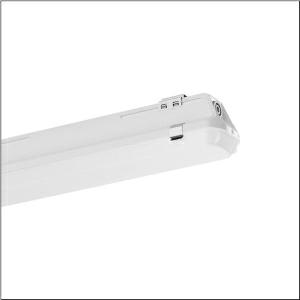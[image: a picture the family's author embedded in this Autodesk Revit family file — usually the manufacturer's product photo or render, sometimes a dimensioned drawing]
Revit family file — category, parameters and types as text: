
# Revit family: monsun_r__11_51fp10ep460h_f2a9
name_source: partatom
category: Lighting Fixtures
units: mm (PartAtom-declared; Revit-internal decimal feet)

## family parameters
Cut with Voids When Loaded = No
Host = Face
Light Source = No
Part Type = Normal
Room Calculation Point = No
Round Connector Dimension = Use Diameter
Shared = No

## types (1)
- --- (1 x LED, 6050 lm, 34.6 W, 4000K)
    Apparent Load = 35 VA
    CIE Flux Codes = 47 77 93 94 100
    Color Rendering = 80
    Color Temperature = 4000K
    Default Elevation = 1800 mm
    Description = Monsun® 11, damp-proof luminaire, chain hanger, primary optical cover: enclosure, of PMMA, light emission: direct distribution, primary light characteristic: symmetric, installation type: suspended mounting, surface-mounted, horizontal mounting, vertical mounting, LED, rated luminous flux: 6.050lm, luminous efficacy: 175lm/W, light colour: 840, colour temperature: 4000K, control gear: ECG DALI, with terminal, 5-pole, max. 2.5mm², mains connection: 220..240V, AC, 50/60Hz, rated input power: 35W, luminaire housing, of glass-fibre reinforced polyester, uncoated, bright grey, incl. chain hanger, length: 1.590mm, width: 90mm, height: 88mm, clip for enclosure, of stainless steel (V2A), ceiling mounting element, of stainless steel (V2A), chain hanger, of stainless steel (V2A), protection rating (complete): IP66, insulation class (complete): insulation class I (protective earthing), certification: CE, ENEC, VDE, UKCA, protection symbol: D, impact resistance: IK04, permissible operating ambient temperature: -25..+40°C, standard: EN 50419, EN 60598-2-1, no direct snow, no direct sun, no direct rain, for indoor or canopied outdoor use, corresponds to IFS (International Featured Standards) requirements for safety and quality in the food industry, contact your sales advisor before using the luminaires in applications with unclear chemical exposure, large temperature fluctuations or condensation-forming humidity, LABS conformity tested according to VDMA 24364:2018-05, packaging unit: 1 piece
    Height = 89 mm
    Lamp = 1 x LED
    Lamp Light Flux = 6050 lm
    Lamp Power = 34.6 W
    Lamp count = 1
    Length = 1590 mm
    Luminous efficacy = 175 lm/W
    Manufacturer = Siteco
    ModVariant = No
    Model = 51FP10EP460H
    Mounting Place = Ceiling
    Mounting Type = Surface mounted
    Number of Poles = 1
    OnlyDefault = Yes
    Power Factor = 1
    Product Name = Monsun® 11
    Product group = damp-proof luminaire
    ProductGroupID = 301
    Protection Class = Protection class I
    Protection Degree = IP 66
    RLX_Detail_Level = 1
    RLX_Emergency_Light_Flux = 0 lm
    RLX_Emergency_Type = 0
    RLX_Emergency_Type_DB = No
    RlxData = <blob elided: 92425 chars, md5=b4d11d01>
    Socket = socket
    Standby Power = 0 W
    System Light Flux = 6050 lm
    System Power = 35 W
    Type Comments = factory setting: luminous flux: 100 % | dim-lin: 254 | 232 mA
    Type Image = l_1004748.jpg
    URL = http://relux.com
    VarID = @adj_157237
    Voltage = 0 V
    Weight = 0.00 kg
    Width = 90 mm

## geometry (parser evidence)
native form markers: Blend x4, Sweep x12
no freeform markers — native parametric forms only
